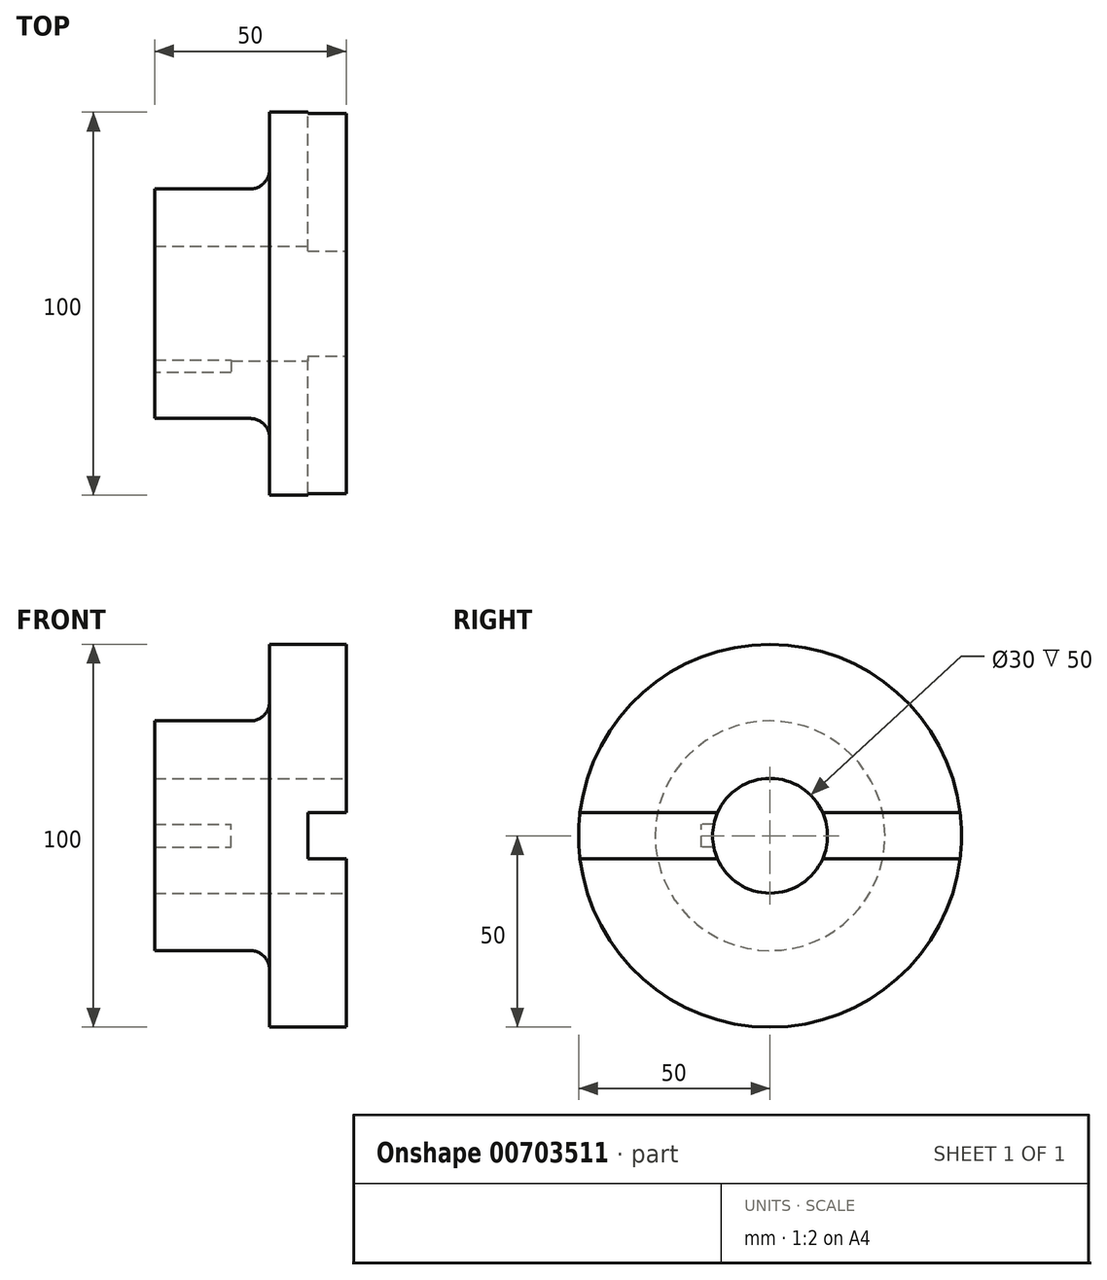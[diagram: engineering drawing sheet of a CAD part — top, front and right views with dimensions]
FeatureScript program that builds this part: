
annotation { "Feature Type Name" : "Feature", "Feature Type Description" : "" }
export const myFeature = defineFeature(function(context is Context, id is Id, definition is map)
    precondition{}
    {
        {
            var Q0;
            Q0=qCreatedBy(makeId("Top.planeOp"),FACE);
            var sketch = newSketch(context, id + "F0", { "sketchPlane" : qUnion([Q0])});
            skLineSegment(sketch, "E0", {"start": v(0, 0) * mm, "end": v(0, 30) * mm});
            skLineSegment(sketch, "E1", {"start": v(0, 30) * mm, "end": v(30, 30) * mm});
            skLineSegment(sketch, "E2", {"start": v(30, 30) * mm, "end": v(30, 50) * mm});
            skLineSegment(sketch, "E3", {"start": v(30, 50) * mm, "end": v(50, 50) * mm});
            skLineSegment(sketch, "E4", {"start": v(50, 50) * mm, "end": v(50, 0) * mm});
            skLineSegment(sketch, "E5", {"start": v(50, 0) * mm, "end": v(0, 0) * mm});
            skLineSegment(sketch, "E6", {"start": v(0, 15) * mm, "end": v(50, 15) * mm});
            skSolve(sketch);
        }
        {
            var Q0;
            {var subQ1=sQuery(id+"F0.wireOp",EDGE,"E1");Q0=makeQuery(id+"F0.imprint","IMPRINT",FACE,{"disambiguationData":[TD([[makeQuery(id+"F0.imprint","IMPRINT",EDGE,{"derivedFrom":subQ1}),-1.0]])]});}
            var Q1;
            Q1=sQuery(id+"F0.wireOp",EDGE,"E5");
            revolve(context, id + "F1", {"surfaceOperationType" : NewSurfaceOperationType.NEW, "entities" : qUnion([Q0]), "axis" : qUnion([Q1]), "revolveType" : RevolveType.FULL});
        }
        {
            var Q0;
            Q0=makeQuery(id+"F1.opRevolve","SWEPT_FACE",FACE,{"disambiguationData":[OSD([sQuery(id+"F0.wireOp",EDGE,"E4")])]});
            var sketch = newSketch(context, id + "F2", { "sketchPlane" : qUnion([Q0])});
            skLineSegment(sketch, "E7.bottom", {"start": v(-55, 6) * mm, "end": v(55, 6) * mm});
            skLineSegment(sketch, "E7.top", {"start": v(-55, -6) * mm, "end": v(55, -6) * mm});
            skLineSegment(sketch, "E7.left", {"start": v(-55, 6) * mm, "end": v(-55, -6) * mm});
            skLineSegment(sketch, "E7.right", {"start": v(55, 6) * mm, "end": v(55, -6) * mm});
            skPoint(sketch, "E7.middle", {"position": v(0, 0) * mm});
            skSolve(sketch);
        }
        {
            var Q0;
            Q0 = qSketchRegion(id + "F2", true);
            extrude(context, id + "F3", {"entities" : qUnion([Q0]), "operationType" : NewBodyOperationType.REMOVE, "oppositeDirection" : true, "depth" : 10 * mm, "offsetDistance" : 25 * mm});
        }
        {
            var Q0;
            Q0=makeQuery(id+"F1.opRevolve","SWEPT_FACE",FACE,{"disambiguationData":[OSD([sQuery(id+"F0.wireOp",EDGE,"E0")])]});
            var sketch = newSketch(context, id + "F4", { "sketchPlane" : qUnion([Q0])});
            skLineSegment(sketch, "E8.bottom", {"start": v(12, -3) * mm, "end": v(18, -3) * mm});
            skLineSegment(sketch, "E8.top", {"start": v(12, 3) * mm, "end": v(18, 3) * mm});
            skLineSegment(sketch, "E8.left", {"start": v(12, -3) * mm, "end": v(12, 3) * mm});
            skLineSegment(sketch, "E8.right", {"start": v(18, -3) * mm, "end": v(18, 3) * mm});
            skPoint(sketch, "E8.middle", {"position": v(15, 0) * mm});
            skSolve(sketch);
        }
        {
            var Q0;
            Q0 = qSketchRegion(id + "F4", true);
            extrude(context, id + "F5", {"entities" : qUnion([Q0]), "operationType" : NewBodyOperationType.REMOVE, "oppositeDirection" : true, "depth" : 20 * mm, "offsetDistance" : 25 * mm});
        }
        {
            var Q0;
            Q0=makeQuery(id+"F1.opRevolve","SWEPT_EDGE",EDGE,{"disambiguationData":[OSD([sQuery(id+"F0.wireOp",EDGE,"E1"),sQuery(id+"F0.wireOp",EDGE,"E2")])]});
            fillet(context, id + "F6", {"entities" : qUnion([Q0]), "radius" : 5 * mm, "tangentPropagation" : true, "allowEdgeOverflow" : false});
        }
    });
